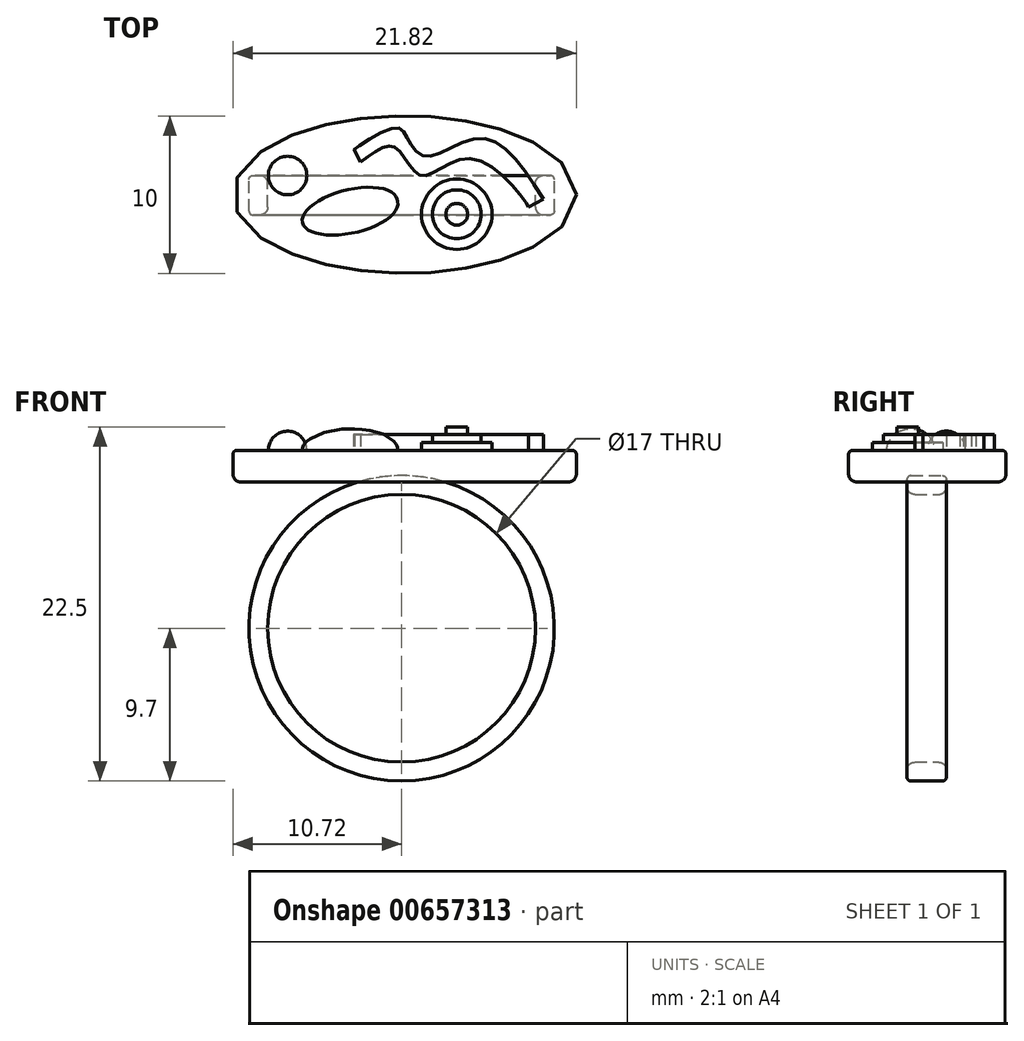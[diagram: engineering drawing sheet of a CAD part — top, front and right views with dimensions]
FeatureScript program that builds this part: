
annotation { "Feature Type Name" : "Feature", "Feature Type Description" : "" }
export const myFeature = defineFeature(function(context is Context, id is Id, definition is map)
    precondition{}
    {
        {
            var Q0;
            Q0=qCreatedBy(makeId("Front.planeOp"),FACE);
            var sketch = newSketch(context, id + "F0", { "sketchPlane" : qUnion([Q0])});
            skCircle(sketch, "E0", {"center": v(0, 0) * mm, "radius": 8.5 * mm});
            skCircle(sketch, "E1.0", {"center": v(0, 0) * mm, "radius": 9.7 * mm});
            skSolve(sketch);
        }
        {
            var Q0;
            Q0 = qSketchRegion(id + "F0", true);
            extrude(context, id + "F1", {"entities" : qUnion([Q0]), "depth" : 2.5 * mm, "offsetDistance" : 25 * mm});
        }
        {
            var Q0;
            Q0=qCreatedBy(makeId("Top.planeOp"),FACE);
            var sketch = newSketch(context, id + "F2", { "sketchPlane" : qUnion([Q0])});
            skEllipse(sketch, "E2", {"center": v(18, 9.19) * mm, "majorRadius": 10.9 * mm, "minorRadius": 5 * mm, "majorAxis": v(1, 0)});
            skSolve(sketch);
        }
        {
            var Q0;
            Q0 = qSketchRegion(id + "F2", true);
            extrude(context, id + "F3", {"entities" : qUnion([Q0]), "depth" : 2 * mm, "offsetDistance" : 25 * mm});
        }
        {
            var Q0;
            Q0=makeQuery(id+"F3.opExtrude","SWEPT_BODY",BODY,{"disambiguationData":[OSD([sQuery(id+"F2.wireOp",EDGE,"E2")])]});
            transform(context, id + "F4", {"entities" : qUnion([Q0]), "transformType" : TransformType.TRANSLATION_3D, "dx" : -17.8 * mm, "dy" : -10.4 * mm, "dz" : 9.3 * mm, "makeCopy" : false});
        }
        {
            var Q0;
            Q0=makeQuery(id+"F3.opExtrude","CAP_FACE",FACE,{"disambiguationData":[OSD([sQuery(id+"F2.wireOp",EDGE,"E2")])],"isStart":false});
            var sketch = newSketch(context, id + "F5", { "sketchPlane" : qUnion([Q0])});
            skCircle(sketch, "E3", {"center": v(-7.24, 0) * mm, "radius": 1.22 * mm});
            skLineSegment(sketch, "E4", {"start": v(-7.24, 1.91) * mm, "end": v(-7.24, -2.06) * mm});
            skSolve(sketch);
        }
        {
            var Q0;
            {var subQ0=sQuery(id+"F5.wireOp",EDGE,"E4");var subQ1=sQuery(id+"F5.wireOp",EDGE,"E3");var subQ2=makeQuery(id+"F5.imprint","INTERSECT",VERTEX,{"disambiguationData":[OD(0.0)],"derivedFrom":[subQ1,subQ0]});Q0=makeQuery(id+"F5.imprint","IMPRINT",FACE,{"disambiguationData":[TD([[makeQuery(id+"F5.imprint","IMPRINT",EDGE,{"disambiguationData":[TD([[subQ2,-1.0]])],"derivedFrom":subQ1}),1.0]])]});}
            var Q1;
            Q1=sQuery(id+"F5.wireOp",EDGE,"E4");
            revolve(context, id + "F6", {"operationType" : NewBodyOperationType.ADD, "entities" : qUnion([Q0]), "axis" : qUnion([Q1]), "revolveType" : RevolveType.FULL});
        }
        {
            var Q0;
            Q0=makeQuery(id+"F3.opExtrude","CAP_FACE",FACE,{"disambiguationData":[OSD([sQuery(id+"F2.wireOp",EDGE,"E2")])],"isStart":false});
            var sketch = newSketch(context, id + "F7", { "sketchPlane" : qUnion([Q0])});
            skEllipse(sketch, "E5", {"center": v(-3.27, -2.33) * mm, "majorRadius": 3.1 * mm, "minorRadius": 1.33 * mm, "majorAxis": v(0.98, 0.21)});
            skLineSegment(sketch, "E6", {"start": v(-6.3, -3) * mm, "end": v(0.54, -1.38) * mm});
            skSolve(sketch);
        }
        {
            var Q0;
            {var subQ0=sQuery(id+"F7.wireOp",EDGE,"E6");var subQ1=sQuery(id+"F7.wireOp",EDGE,"E5");var subQ2=makeQuery(id+"F7.imprint","INTERSECT",VERTEX,{"disambiguationData":[OD(0.0)],"derivedFrom":[subQ1,subQ0]});Q0=makeQuery(id+"F7.imprint","IMPRINT",FACE,{"disambiguationData":[TD([[makeQuery(id+"F7.imprint","IMPRINT",EDGE,{"disambiguationData":[TD([[subQ2,1.0]])],"derivedFrom":subQ1}),1.0]])]});}
            var Q1;
            Q1=sQuery(id+"F7.wireOp",EDGE,"E6");
            revolve(context, id + "F8", {"operationType" : NewBodyOperationType.ADD, "entities" : qUnion([Q0]), "axis" : qUnion([Q1]), "revolveType" : RevolveType.FULL});
        }
        {
            var Q0;
            Q0=makeQuery(id+"F3.opExtrude","CAP_FACE",FACE,{"disambiguationData":[OSD([sQuery(id+"F2.wireOp",EDGE,"E2")])],"isStart":false});
            var sketch = newSketch(context, id + "F9", { "sketchPlane" : qUnion([Q0])});
            skFitSpline(sketch, "E7", {"points": [v(-2.6, 0.85) * mm, v(-0.4, 1.78) * mm, v(1.23, 0) * mm, v(4.64, 1.05) * mm, v(8.08, -2.07) * mm, v(8.01, -2.04) * mm, v(8.05, -2.04) * mm], "startDerivative": vector(11.82, 9.3) * mm, "endDerivative": vector(2.16, -0.46) * mm});
            skLineSegment(sketch, "E8", {"start": v(8.03, -2.03) * mm, "end": v(9, -1.49) * mm});
            skFitSpline(sketch, "E9", {"points": [v(9, -1.49) * mm, v(5.06, 2.38) * mm, v(1.56, 1.22) * mm, v(0.33, 2.43) * mm, v(-0.46, 3.03) * mm, v(-3.04, 1.6) * mm, v(-2.98, 1.6) * mm], "startDerivative": vector(-13.37, 20.95) * mm, "endDerivative": vector(3.42, 0.74) * mm});
            skLineSegment(sketch, "E10", {"start": v(-2.98, 1.6) * mm, "end": v(-2.6, 0.85) * mm});
            skSolve(sketch);
        }
        {
            var Q0;
            Q0 = qSketchRegion(id + "F9", true);
            extrude(context, id + "F10", {"entities" : qUnion([Q0]), "operationType" : NewBodyOperationType.ADD, "depth" : 1 * mm, "offsetDistance" : 25 * mm});
        }
        {
            var Q0;
            Q0=makeQuery(id+"F3.opExtrude","CAP_FACE",FACE,{"disambiguationData":[OSD([sQuery(id+"F2.wireOp",EDGE,"E2")])],"isStart":false});
            var sketch = newSketch(context, id + "F11", { "sketchPlane" : qUnion([Q0])});
            skCircle(sketch, "E11", {"center": v(3.5, -2.46) * mm, "radius": 2.24 * mm});
            skSolve(sketch);
        }
        {
            var Q0;
            Q0=makeQuery(id+"F11.imprint","IMPRINT",FACE,{"disambiguationData":[TD([[makeQuery(id+"F11.imprint","IMPRINT",EDGE,{"derivedFrom":sQuery(id+"F11.wireOp",EDGE,"E11")}),1.0]])]});
            extrude(context, id + "F12", {"entities" : qUnion([Q0]), "operationType" : NewBodyOperationType.ADD, "depth" : .5 * mm, "offsetDistance" : 25 * mm});
        }
        {
            var Q0;
            Q0=makeQuery(id+"F12.opExtrude","CAP_FACE",FACE,{"disambiguationData":[OSD([sQuery(id+"F11.wireOp",EDGE,"E11")])],"isStart":false});
            var sketch = newSketch(context, id + "F13", { "sketchPlane" : qUnion([Q0])});
            skCircle(sketch, "E12", {"center": v(3.5, -2.46) * mm, "radius": 1.55 * mm});
            skSolve(sketch);
        }
        {
            var Q0;
            Q0 = qSketchRegion(id + "F13", true);
            extrude(context, id + "F14", {"entities" : qUnion([Q0]), "operationType" : NewBodyOperationType.ADD, "depth" : .5 * mm, "offsetDistance" : 25 * mm});
        }
        {
            var Q0;
            Q0=makeQuery(id+"F14.opExtrude","CAP_FACE",FACE,{"disambiguationData":[OSD([sQuery(id+"F13.wireOp",EDGE,"E12")])],"isStart":false});
            var sketch = newSketch(context, id + "F15", { "sketchPlane" : qUnion([Q0])});
            skCircle(sketch, "E13", {"center": v(3.5, -2.46) * mm, "radius": 0.69 * mm});
            skSolve(sketch);
        }
        {
            var Q0;
            Q0=makeQuery(id+"F15.imprint","IMPRINT",FACE,{"disambiguationData":[TD([[makeQuery(id+"F15.imprint","IMPRINT",EDGE,{"derivedFrom":sQuery(id+"F15.wireOp",EDGE,"E13")}),1.0]])]});
            extrude(context, id + "F16", {"entities" : qUnion([Q0]), "operationType" : NewBodyOperationType.ADD, "depth" : .5 * mm, "offsetDistance" : 25 * mm});
        }
        {
            var Q0;
            Q0=makeQuery(id+"F1.opExtrude","CAP_EDGE",EDGE,{"disambiguationData":[OSD([sQuery(id+"F0.wireOp",EDGE,"E0")])],"isStart":false});
            var Q1;
            Q1=makeQuery(id+"F1.opExtrude","CAP_EDGE",EDGE,{"disambiguationData":[OSD([sQuery(id+"F0.wireOp",EDGE,"E0")])],"isStart":true});
            fillet(context, id + "F17", {"entities" : qUnion([Q0, Q1]), "radius" : .5 * mm, "tangentPropagation" : true, "allowEdgeOverflow" : false});
        }
        {
            var Q0;
            Q0=makeQuery(id+"F3.opExtrude","CAP_EDGE",EDGE,{"disambiguationData":[OSD([sQuery(id+"F2.wireOp",EDGE,"E2")])],"isStart":true});
            fillet(context, id + "F18", {"entities" : qUnion([Q0]), "radius" : .5 * mm, "tangentPropagation" : true, "allowEdgeOverflow" : false});
        }
        {
            var Q0;
            Q0=makeQuery(id+"F1.opExtrude","CAP_EDGE",EDGE,{"disambiguationData":[OSD([sQuery(id+"F0.wireOp",EDGE,"E1.0")])],"isStart":false});
            var Q1;
            Q1=makeQuery(id+"F1.opExtrude","CAP_EDGE",EDGE,{"disambiguationData":[OSD([sQuery(id+"F0.wireOp",EDGE,"E1.0")])],"isStart":true});
            fillet(context, id + "F19", {"entities" : qUnion([Q0, Q1]), "radius" : .25 * mm, "tangentPropagation" : true, "allowEdgeOverflow" : false});
        }
        {
            var Q0;
            Q0=makeQuery(id+"F3.opExtrude","CAP_EDGE",EDGE,{"disambiguationData":[OSD([sQuery(id+"F2.wireOp",EDGE,"E2")])],"isStart":false});
            fillet(context, id + "F20", {"entities" : qUnion([Q0]), "radius" : .25 * mm, "tangentPropagation" : true, "allowEdgeOverflow" : false});
        }
    });
